# Revit family: RUFO2 290xWSxZ0150xx
name_source: partatom
category: Leuchten
units: mm (PartAtom-declared; Revit-internal decimal feet)

## family parameters
Basisbauteil = Fläche
Beim Laden mit Abzugskörper schneiden = Nein
Bemaßung runder Anschluss = Durchmesser verwenden
Gemeinsam genutzt = Nein
Lichtquelle = Ja
OmniClass-Nummer = 23.80.70.11
OmniClass-Titel = Luminaries for Internal Lighting
Raumberechnungspunkt = Nein
Teiletyp = Normal

## types (18) — shared parameters
Baugruppenkennzeichen = D5020200
Datei für fotometrisches Netz = RUFO2_290_Z.IES
Emissionsform beim Rendern sichtbar = Nein
Farbfilter = 16777215
Farbtemperaturverschiebung bei Dämpfen der Lampe = <Keine Auswahl>
Hersteller = RIDI Leuchten GmbH
Lampe = LED
Neigungswinkel = 90.00°
Scheinlast = 10 VA
URL = www.ridi.de
Von Kreisdurchmesser aussenden = 290 mm  [stored 0.951444 ft]
brand = RIDI
conformity mark = CE
electrical safety class = 1
height = 70 mm  [stored 0.229659 ft]
ingress protection (IP) code = IP40
length = 290 mm  [stored 0.951444 ft]
nominal frequency = 50-60Hz
nominal voltage = 230
rated input power = 10
voltage type (AC, DC, UC) = AC
width = 290 mm  [stored 0.951444 ft]
zero-valued in all types: Vorgabe-Ansicht

## per-type parameters (varying)
| type | Modell | weight |
| RUFO2 290NDWS840Z0150 | 0420865 | 0.9 kg |
| RUFO2 290NDWS840Z0150-RS | 0420865//396 | 0.95 kg |
| RUFO2 290NDWS840Z0150-2K | 0420866 | 1.0 kg |
| RUFO2 290NDWS830Z0150 | 0420871 | 0.9 kg |
| RUFO2 290NDWS830Z0150-RS | 0420871//396 | 0.95 kg |
| RUFO2 290NDWS830Z0150-2K | 0420872 | 1.0 kg |
| RUFO2 290NDWS840Z0150-IK | 0420877 | 0.9 kg |
| RUFO2 290NDWS840Z0150-IK-EDS3 | 0420877//377 | 1.1 kg |
| RUFO2 290NDWS840Z0150-IK-RS | 0420877//396 | 0.95 kg |
| RUFO2 290NDWS840Z0150-IK-2K | 0420878 | 1.0 kg |
| RUFO2 290NDWS830Z0150-IK | 0420883 | 0.9 kg |
| RUFO2 290NDWS830Z0150-IK-EDS3 | 0420883//377 | 1.1 kg |
| RUFO2 290NDWS830Z0150-IK-RS | 0420883//396 | 0.95 kg |
| RUFO2 290NDWS830Z0150-IK-2K | 0420884 | 1.0 kg |
| RUFO2 290DAWS840Z0150 | 0430865 | 0.95 kg |
| RUFO2 290DAWS830Z0150 | 0430871 | 0.95 kg |
| RUFO2 290DAWS840Z0150-IK | 0430877 | 0.95 kg |
| RUFO2 290DAWS830Z0150-IK | 0430883 | 0.95 kg |

note: column(s) folded — value = type name in every type: product name

note: [stored X ft] marks values corroborated as IEEE doubles in the binary element streams (Revit-internal decimal feet)
